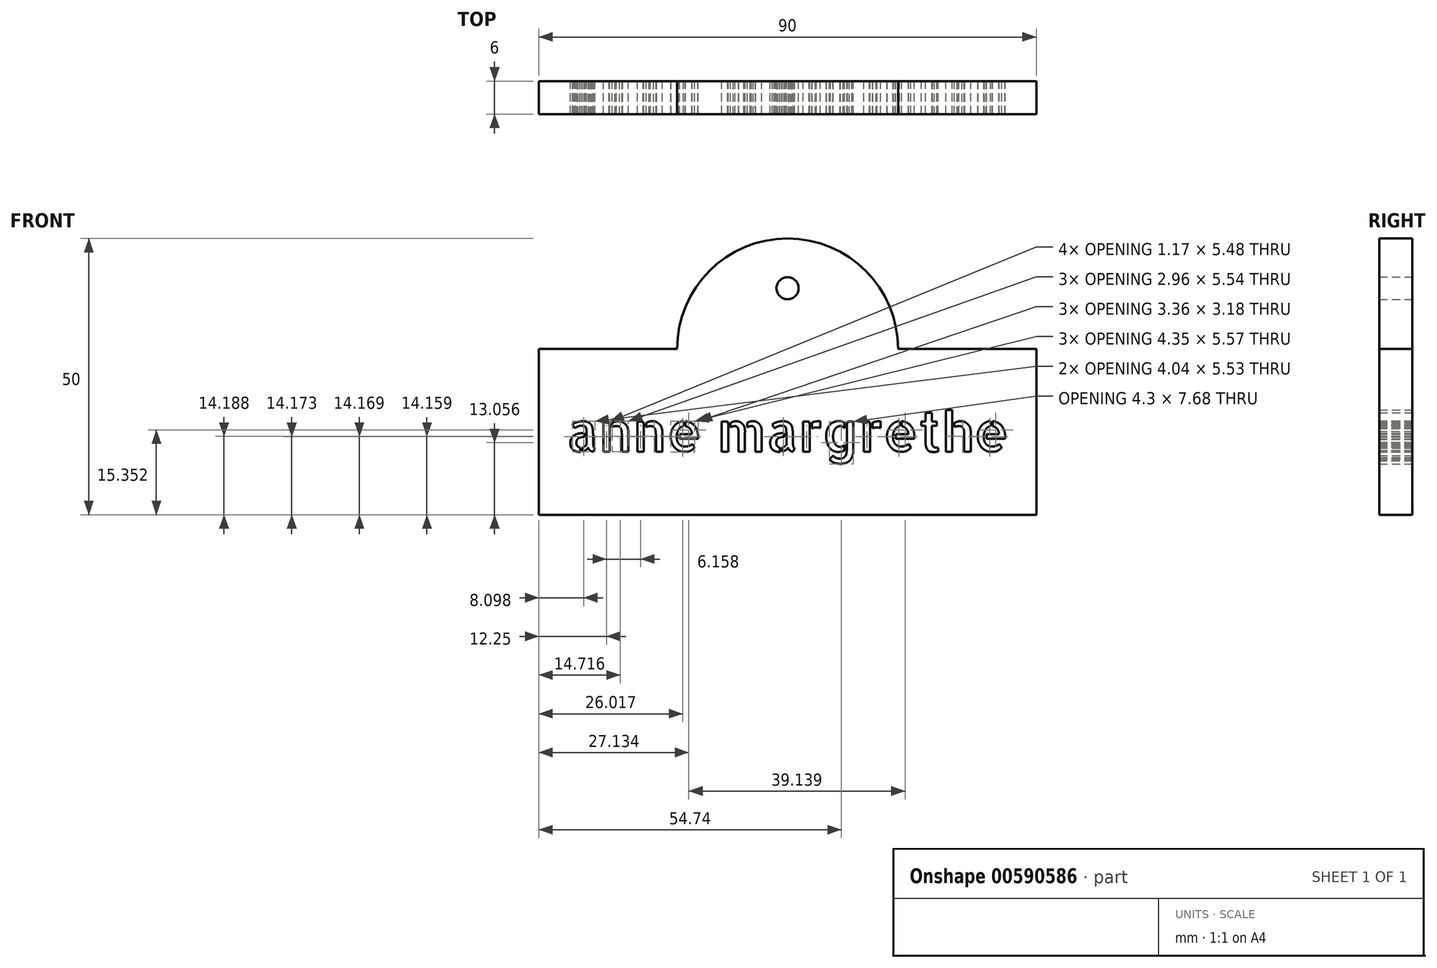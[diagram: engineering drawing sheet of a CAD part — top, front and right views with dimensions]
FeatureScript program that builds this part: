
annotation { "Feature Type Name" : "Feature", "Feature Type Description" : "" }
export const myFeature = defineFeature(function(context is Context, id is Id, definition is map)
    precondition{}
    {
        {
            var Q0;
            Q0=qCreatedBy(makeId("Front.planeOp"),FACE);
            var sketch = newSketch(context, id + "F0", { "sketchPlane" : qUnion([Q0])});
            skLineSegment(sketch, "E0.bottom", {"start": v(-42.78, 29.91) * mm, "end": v(-17.78, 29.91) * mm});
            skLineSegment(sketch, "E0.top", {"start": v(-42.78, -0.09) * mm, "end": v(47.22, -0.09) * mm});
            skLineSegment(sketch, "E0.left", {"start": v(-42.78, 29.91) * mm, "end": v(-42.78, -0.09) * mm});
            skLineSegment(sketch, "E0.right", {"start": v(47.22, 29.91) * mm, "end": v(47.22, -0.09) * mm});
            skArc(sketch, "E1", {"start": v(22.22, 29.91) * mm, "mid": v(2.22, 49.91) * mm, "end": v(-17.78, 29.91) * mm});
            skCircle(sketch, "E2", {"center": v(2.22, 40.91) * mm, "radius": 2 * mm});
            skLineSegment(sketch, "E3.trimOffspring", {"start": v(22.22, 29.91) * mm, "end": v(47.22, 29.91) * mm});
            skText(sketch, "E4", { "text": "anne margrethe\n", "fontName": "AllertaStencil-Regular.ttf"});
            skPoint(sketch, "E5", {"position": v(2.22, 49.91) * mm});
            skPoint(sketch, "E6", {"position": v(2.22, 18.49) * mm});
            skPoint(sketch, "E7", {"position": v(47.22, 14.91) * mm});
            skPoint(sketch, "E8", {"position": v(42.22, 14.91) * mm});
            const initialGuessF0  = {"E4": [-0.03778, 0.01133, 1, 0, 0.00716]};
            skSetInitialGuess(sketch, initialGuessF0);
            skSolve(sketch);
        }
        {
            var Q0;
            Q0=makeQuery(id+"F0.imprint","IMPRINT",FACE,{"disambiguationData":[TD([[makeQuery(id+"F0.imprint","IMPRINT",EDGE,{"derivedFrom":sQuery(id+"F0.wireOp",EDGE,"E0.bottom")}),-1.0]])]});
            extrude(context, id + "F1", {"entities" : qUnion([Q0]), "depth" : 6 * mm, "offsetDistance" : 25 * mm});
        }
    });
